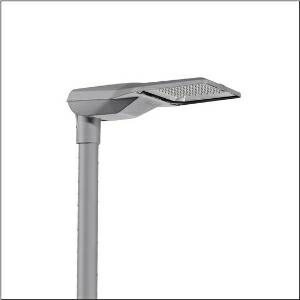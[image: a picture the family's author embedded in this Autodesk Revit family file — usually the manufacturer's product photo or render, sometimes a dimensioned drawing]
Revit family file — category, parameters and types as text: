
# Revit family: streetlight_sl_21_iq_midi___st0_8a_5xe3c21d08nb_9e73
name_source: partatom
category: Lighting Fixtures
units: mm (PartAtom-declared; Revit-internal decimal feet)

## family parameters
Cut with Voids When Loaded = No
Host = Face
Light Source = No
Part Type = Normal
Room Calculation Point = No
Round Connector Dimension = Use Diameter
Shared = No

## types (1)
- --- (1 x LED, 19210 lm, 155.5 W, 2200K)
    Apparent Load = 155 VA
    CIE Flux Codes = 41 75 97 100 100
    Color Rendering = 70
    Color Temperature = 2200K
    Default Elevation = 1800 mm
    Description = Streetlight SL 21 iQ midi, mast luminaire, primary light control with lens, of PMMA, primary optical cover: cover, of toughened safety glass, transparent, light distribution: ST0.8a, light emission: direct distribution, primary light characteristic: asymmetric, installation type: post-top, side-entry, LED, High Power LED, rated luminous flux: 19.210lm, luminous efficacy: 124lm/W, light colour: 722, colour temperature: 2200K, control gear: iQ-Comfort, control: Auto-Match, Temp-Guard, Lumen-Switch, Night-Set, Smart-Wire, Light-Fading, Desk-Remote (wireless, voltage-free reading and setting of iQ features in the workshop via application-optimized NFC function/RFID function), optimised constant luminous flux control (CLO 2.0), pre-setting: linear dimming characteristic, mains connection: 230..240V, AC, 50/60Hz, start of lifetime: 156W, end of service life: 162W, reduction: 69W, luminaire housing, of diecast aluminium, powder-coated, SITECO metallic grey (DB 702S), corrosivity category C5 high according to DIN EN ISO 12944, please order mast flange separately, inclination adjustable: 0°, 5°, 10°, 15°, sealing non-destructively replaceable, multi-level sealing system, length: 644mm, width: 335mm, height: 110mm, mast flange for spigot size: 42mm (side-entry): 5XC10008XM4, 60/48mm (side-entry/post-top): 5XC10108XM2, 76/60mm (side-entry/post-top): 5XC10108XM1, mounting height: 4..8m, protection rating (complete): IP66, insulation class (complete): insulation class II (safety insulation), certification: CE, ENEC, ENEC+, VDE, impact resistance: IK10, permissible operating ambient temperature for outdoor applications: -40..+50°C, standard-compliant lighting for roads and squares, packaging unit: 1 piece

Light Distribution: ST0.8a
    Height = 111 mm
    Lamp = 1 x LED
    Lamp Light Flux = 19210 lm
    Lamp Power = 155.5 W
    Lamp count = 1
    Length = 644 mm
    Luminous efficacy = 124 lm/W
    Manufacturer = Siteco
    ModVariant = No
    Model = 5XE3C21D08NB
    Number of Poles = 1
    OnlyDefault = Yes
    Power Factor = 1
    Product Name = Streetlight SL 21 iQ midi | ST0.8a
    Product group = mast luminaire | pylon top
    ProductGroupID = 6100
    Protection Class = Protection class II
    Protection Degree = IP 66
    RLX_Detail_Level = 1
    RLX_Emergency_Light_Flux = 0 lm
    RLX_Emergency_Type = 0
    RLX_Emergency_Type_DB = No
    RlxData = <blob elided: 27217 chars, md5=3be17c41>
    Socket = socket
    Standby Power = 0 W
    System Light Flux = 19210 lm
    System Power = 155 W
    Type Comments = factory setting: luminous flux: 100 % | dim-lin: 254 | 823 mA
    Type Image = l_1004298.jpg
    URL = http://relux.com
    VarID = @adj_168553
    Voltage = 0 V
    Weight = 0.00 kg
    Width = 336 mm

## geometry (parser evidence)
native form markers: Blend x4, Sweep x11
no freeform markers — native parametric forms only
